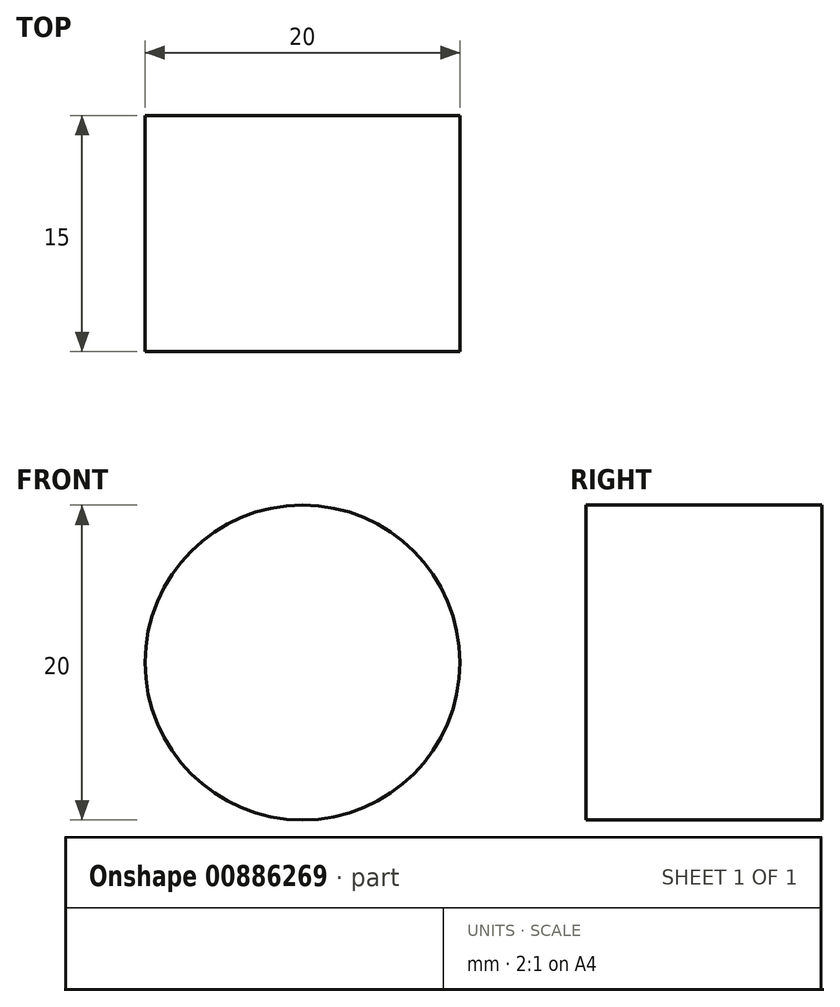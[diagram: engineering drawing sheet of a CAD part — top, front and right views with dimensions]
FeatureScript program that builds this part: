
annotation { "Feature Type Name" : "Feature", "Feature Type Description" : "" }
export const myFeature = defineFeature(function(context is Context, id is Id, definition is map)
    precondition{}
    {
        {
            var Q0;
            Q0=qCreatedBy(makeId("Front.planeOp"),FACE);
            var sketch = newSketch(context, id + "F0", { "sketchPlane" : qUnion([Q0])});
            skCircle(sketch, "E0", {"center": v(0, 0) * mm, "radius": 10 * mm});
            skSolve(sketch);
        }
        {
            var Q0;
            Q0 = qSketchRegion(id + "F0", true);
            extrude(context, id + "F1", {"entities" : qUnion([Q0]), "depth" : 15 * mm, "offsetDistance" : 25 * mm, "symmetric" : true});
        }
    });
